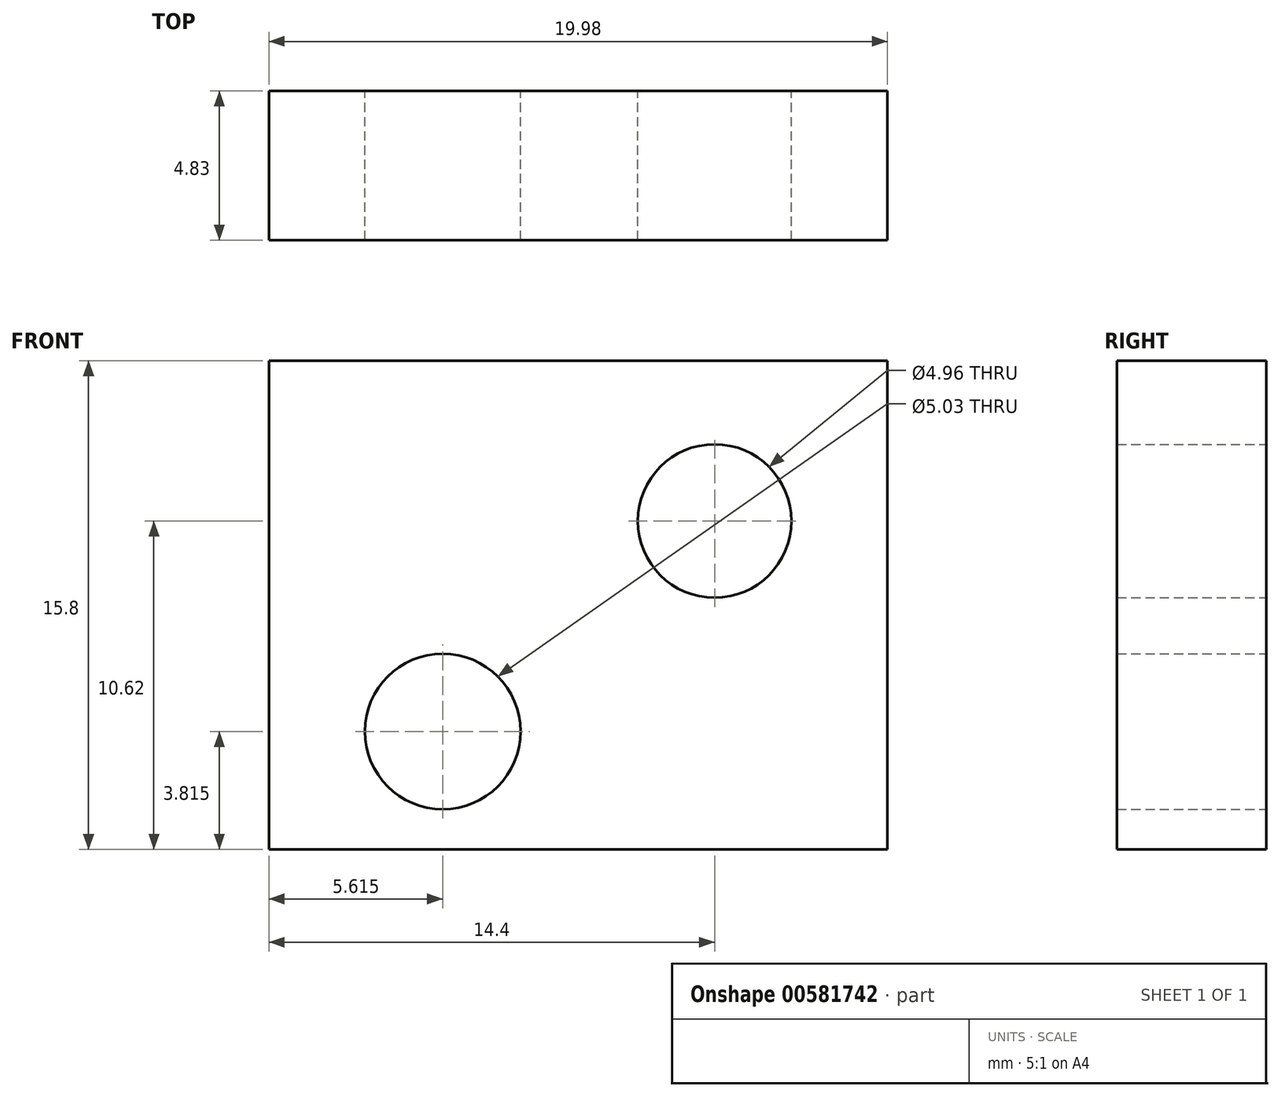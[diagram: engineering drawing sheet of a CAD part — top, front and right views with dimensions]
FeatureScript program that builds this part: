
annotation { "Feature Type Name" : "Feature", "Feature Type Description" : "" }
export const myFeature = defineFeature(function(context is Context, id is Id, definition is map)
    precondition{}
    {
        {
            var Q0;
            Q0=qCreatedBy(makeId("Front.planeOp"),FACE);
            var sketch = newSketch(context, id + "F0", { "sketchPlane" : qUnion([Q0])});
            skLineSegment(sketch, "E0.bottom", {"start": v(0, 0) * mm, "end": v(19.98, 0) * mm});
            skLineSegment(sketch, "E0.top", {"start": v(0, 15.8) * mm, "end": v(19.98, 15.8) * mm});
            skLineSegment(sketch, "E0.left", {"start": v(0, 0) * mm, "end": v(0, 15.8) * mm});
            skLineSegment(sketch, "E0.right", {"start": v(19.98, 0) * mm, "end": v(19.98, 15.8) * mm});
            skCircle(sketch, "E1", {"center": v(14.4, 10.62) * mm, "radius": 2.48 * mm});
            skCircle(sketch, "E2", {"center": v(5.62, 3.82) * mm, "radius": 2.52 * mm});
            skSolve(sketch);
        }
        {
            var Q0;
            Q0 = qSketchRegion(id + "F0", true);
            extrude(context, id + "F1", {"entities" : qUnion([Q0]), "depth" : 4.83 * mm, "offsetDistance" : 25 * mm});
        }
    });
